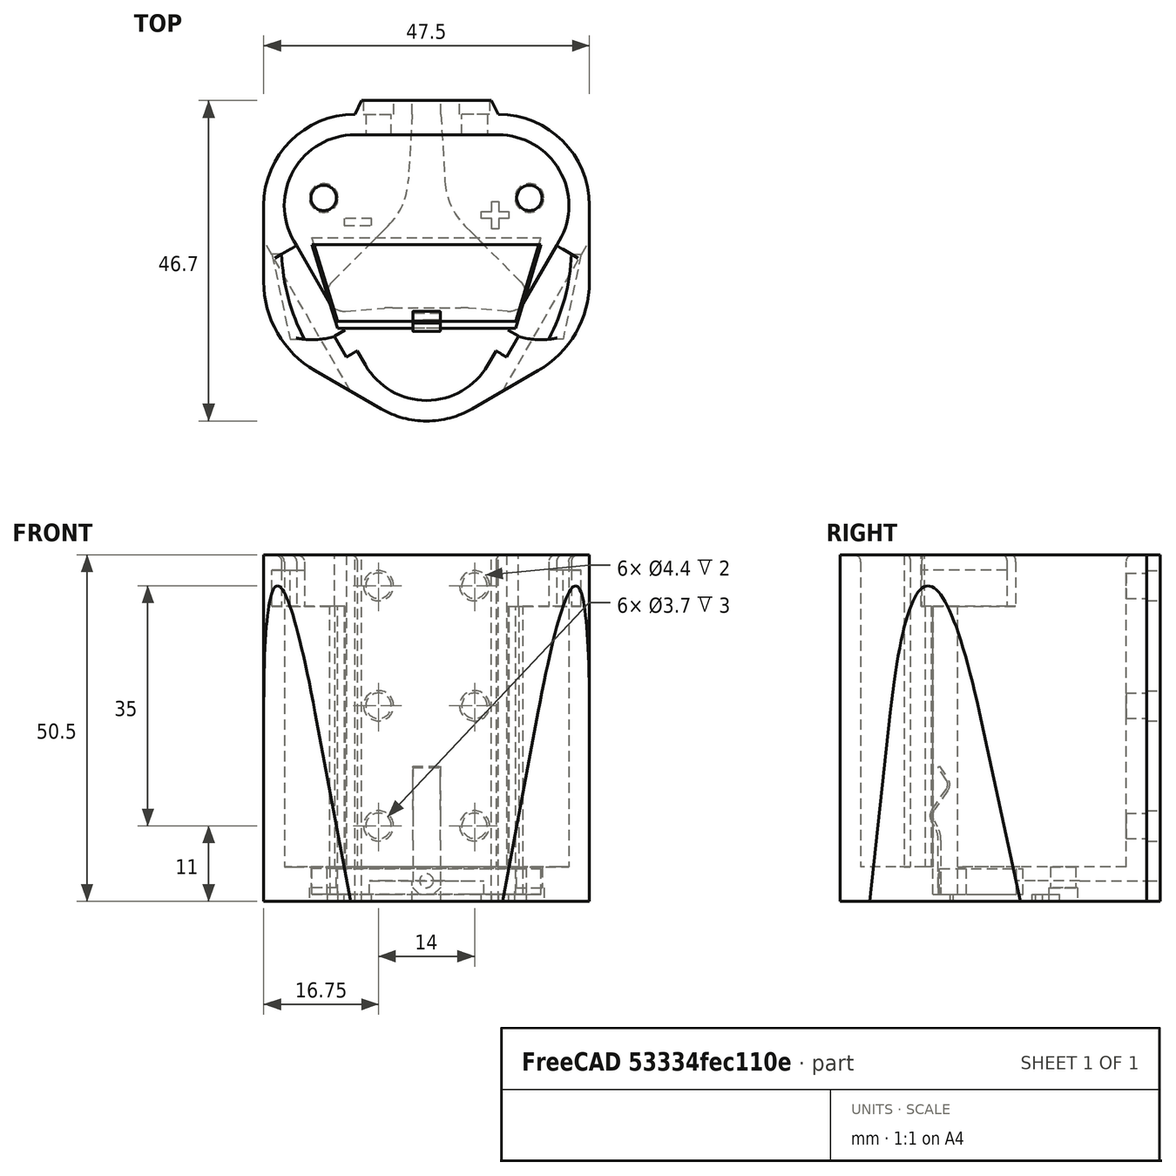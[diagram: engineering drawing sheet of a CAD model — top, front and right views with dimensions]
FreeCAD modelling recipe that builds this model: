
FCSTD DOCUMENT  (FreeCAD 1.0R39319 (Git))
Label: support_batterie_parkside_12V
License: All rights reserved
LicenseURL: https://en.wikipedia.org/wiki/All_rights_reserved
objects: Sketcher::SketchObject×15, PartDesign::Pocket×14, PartDesign::Pad×4, Mesh::Feature×4, PartDesign::Body×3, App::Part×3, PartDesign::Chamfer×2, PartDesign::Mirrored×2, App::LinkElement×2, App::Link×1, PartDesign::SubShapeBinder×1, PartDesign::LinearPattern×1, PartDesign::Fillet×1
note: 103 computed .brp shape members not serialized (recipe doc carries the construction recipe); baked Part::Feature solids carry a one-line shape summary decoded from their .brp

FEATURE [Sketcher::SketchObject] Sketch
  ArcFitTolerance = 1e-06
  AttachmentSupport = -> [XY_Plane003]
  FullyConstrained = true
  MakeInternals = false
  MapMode = 5
  expr: Constraints[10] = 26 / 2
  expr: Constraints[9] = 33.4 / 2
  sketch-geometry (4):
    g0: LineSegment StartX=0 StartY=0 StartZ=0 EndX=-13 EndY=0 EndZ=0
    g1: LineSegment StartX=-13 StartY=0 StartZ=0 EndX=-16.7 EndY=12.2 EndZ=0
    g2: LineSegment StartX=-16.7 StartY=12.2 StartZ=0 EndX=0 EndY=12.2 EndZ=0
    g3: LineSegment StartX=0 StartY=12.2 StartZ=0 EndX=0 EndY=0 EndZ=0
  constraints (11):
    c: Coincident(g-1,g0)
    c: PointOnObject(g0,g-1)
    c: Coincident(g0,g1)
    c: Coincident(g1,g2)
    c: PointOnObject(g2,g-2)
    c: Horizontal(g2)
    c: Coincident(g2,g3)
    c: Coincident(g3,g0)
    c: DistanceY(g3,g3) = 12.2
    c: DistanceX(g2,g2) = 16.7
    c: DistanceX(g0,g0) = 13
FEATURE [PartDesign::Pad] Pad
  Direction = (0,0,1)
  Length = 3.8
  Length2 = 10
  Profile = -> Sketch
  ReferenceAxis = -> Sketch [N_Axis]
  Suppressed = false
  Type = 0
FEATURE [Sketcher::SketchObject] Sketch001
  ArcFitTolerance = 1e-06
  AttachmentSupport = -> [YZ_Plane004]
  FullyConstrained = true
  MakeInternals = false
  MapMode = 5
  Placement = pos=(0,0,0) rot=(0.57735,0.57735,0.57735;2.0944rad)
  sketch-geometry (22):
    g0: LineSegment StartX=-0.2 StartY=0 StartZ=0 EndX=-0.2 EndY=7.9282 EndZ=0
    g1: LineSegment StartX=-0.735898 StartY=9.9282 StartZ=0 EndX=-1.2 EndY=10.7321 EndZ=0
    g2: LineSegment StartX=-1.12969 StartY=12.3424 StartZ=0 EndX=0.965775 EndY=15.335 EndZ=0
    g3: LineSegment StartX=0.980132 StartY=16.6827 StartZ=0 EndX=-0.255119 EndY=18.5293 EndZ=0
    g4: LineSegment StartX=-0.255119 StartY=18.5293 StartZ=0 EndX=0 EndY=18.7 EndZ=0
    g5: LineSegment StartX=0 StartY=18.7 StartZ=0 EndX=1.23525 EndY=16.8534 EndZ=0
    g6: LineSegment StartX=1.2172 StartY=15.159 StartZ=0 EndX=-0.728007 EndY=12.381 EndZ=0
    g7: LineSegment StartX=-0.8 StartY=10.7321 StartZ=0 EndX=-0.335898 EndY=9.9282 EndZ=0
    g8: LineSegment StartX=0.2 StartY=7.9282 StartZ=0 EndX=0.2 EndY=0 EndZ=0
    g9: LineSegment StartX=-0.2 StartY=0 StartZ=0 EndX=0.2 EndY=0 EndZ=0
    g10: ArcOfCircle CenterX=-3.8 CenterY=7.9282 CenterZ=0 NormalX=0 NormalY=0 NormalZ=1 AngleXU=0 Radius=4 StartAngle=0 EndAngle=0.523599
    g11: GeomPoint [constr] X=0.2 Y=9 Z=0
    g12: ArcOfCircle CenterX=-4.2 CenterY=7.9282 CenterZ=0 NormalX=0 NormalY=0 NormalZ=1 AngleXU=0 Radius=4 StartAngle=1e-16 EndAngle=0.523599
    g13: GeomPoint [constr] X=-0.2 Y=9 Z=0
    g14: ArcOfCircle CenterX=0.530127 CenterY=11.5 CenterZ=0 NormalX=0 NormalY=0 NormalZ=1 AngleXU=0 Radius=1.5359 StartAngle=2.53073 EndAngle=3.66519
    g15: GeomPoint [constr] X=-1.28924 Y=11.5794 Z=0
    g16: ArcOfCircle CenterX=0.0990381 CenterY=11.4821 CenterZ=0 NormalX=0 NormalY=0 NormalZ=1 AngleXU=0 Radius=1.5 StartAngle=2.53073 EndAngle=3.66519
    g17: GeomPoint [constr] X=-1.6778 Y=11.5596 Z=0
    g18: ArcOfCircle CenterX=-0.0115278 CenterY=16.0194 CenterZ=0 NormalX=0 NormalY=0 NormalZ=1 AngleXU=0 Radius=1.5 StartAngle=5.67232 EndAngle=6.87274
    g19: GeomPoint [constr] X=1.80608 Y=16 Z=0
    g20: ArcOfCircle CenterX=-0.0115278 CenterY=16.0194 CenterZ=0 NormalX=0 NormalY=0 NormalZ=1 AngleXU=0 Radius=1.19307 StartAngle=5.67232 EndAngle=6.87274
    g21: GeomPoint [constr] X=1.43415 Y=16.004 Z=0
  constraints (53):
    c: PointOnObject(g0,g-1)
    c: Vertical(g0)
    c: Coincident(g3,g4)
    c: Coincident(g4,g5)
    c: Vertical(g8)
    c: Coincident(g0,g9)
    c: Coincident(g9,g8)
    c: Symmetric(g8,g0,g-1)
    c: Horizontal(g11,g13)
    c: PointOnObject(g11,g7)
    c: PointOnObject(g11,g8)
    c: Tangent(g7,g10) = 1.5708
    c: Tangent(g8,g10) = 1.5708
    c: PointOnObject(g13,g1)
    c: PointOnObject(g13,g0)
    c: Tangent(g1,g12) = -1.5708
    c: Tangent(g0,g12) = -1.5708
    c: PointOnObject(g15,g6)
    c: PointOnObject(g15,g7)
    c: Tangent(g6,g14) = -1.5708
    c: Tangent(g7,g14) = -1.5708
    c: PointOnObject(g17,g2)
    c: PointOnObject(g17,g1)
    c: Tangent(g2,g16) = 1.5708
    c: Tangent(g1,g16) = 1.5708
    c: PointOnObject(g19,g5)
    c: PointOnObject(g19,g6)
    c: Tangent(g5,g18) = 1.5708
    c: Tangent(g6,g18) = 1.5708
    c: PointOnObject(g21,g3)
    c: PointOnObject(g21,g2)
    c: Tangent(g3,g20) = -1.5708
    c: Tangent(g2,g20) = -1.5708
    c: Perpendicular(g3,g4)
    c: Equal(g5,g3)
    c: Equal(g7,g1)
    c: Equal(g8,g0)
    c: DistanceY(g0,g4) = 18.7
    c: DistanceY(g-1,g11) = 9
    c: Parallel(g6,g2)
    c: Parallel(g1,g7)
    c: DistanceX(g9,g9) = 0.4
    c: Horizontal(g18,g20)
    c: Perpendicular(g4,g5)
    c: PointOnObject(g4,g-2)
    c: Radius(g18) = 1.5
    c: Radius(g16) = 1.5
    c: Radius(g10) = 4
    c: DistanceY(g-1,g14) = 11.5
    c: DistanceY(g-1,g19) = 16
    c: DistanceX(g1,g-1) = 1.2
    c: Angle(g1,g0) = 2.61799
    c: Angle(g7,g6) = 2.00713
FEATURE [PartDesign::Pad] Pad001
  Direction = (1,0,0)
  Length = 4
  Length2 = 10
  Midplane = true
  Placement = pos=(0,0,0) rot=(1,1,1;2.0944rad)
  Profile = -> Sketch001
  ReferenceAxis = -> Sketch001 [N_Axis]
  Suppressed = false
  Type = 0
FEATURE [Sketcher::SketchObject] Sketch002
  ArcFitTolerance = 1e-06
  AttachmentSupport = -> [Pad001]
  FullyConstrained = true
  MakeInternals = false
  MapMode = 5
  Placement = pos=(0,0.2,0) rot=(0.57735,0.57735,0.57735;4.18879rad)
  sketch-geometry (1):
    g0: Circle CenterX=2 CenterY=0 CenterZ=0 NormalX=0 NormalY=0 NormalZ=1 AngleXU=0 Radius=1
  constraints (3):
    c: PointOnObject(g0,g-1)
    c: Diameter(g0) = 2
    c: DistanceX(g-1,g0) = 2
FEATURE [PartDesign::Pocket] Pocket
  BaseFeature = -> Pad001
  Direction = (0,-1,0)
  Length = 5
  Length2 = 5
  Placement = pos=(0,0,0) rot=(1,1,1;2.0944rad)
  Profile = -> Sketch002
  ReferenceAxis = -> Sketch002 [N_Axis]
  Suppressed = false
  Type = 0
FEATURE [PartDesign::Chamfer] Chamfer
  Angle = 45
  Base = -> Pocket [Edge23,Edge9]
  BaseFeature = -> Pocket
  ChamferType = 0
  FlipDirection = false
  Placement = pos=(0,0,0) rot=(1,1,1;2.0944rad)
  Size = 1
  Size2 = 1
  SupportTransform = false
  Suppressed = false
  UseAllEdges = false
FEATURE [PartDesign::Body] Body001  label="electrode"
  AllowCompound = false
  Group = -> [Sketch001,Pad001,Sketch002,Pocket,Chamfer]
  Origin = -> Origin004
  Tip = -> Chamfer
FEATURE [PartDesign::Mirrored] Mirrored
  BaseFeature = -> Pad
  MirrorPlane = -> Sketch [V_Axis]
  Originals = -> [Pad]
  Refine = true
  Suppressed = false
  TransformMode = 0
FEATURE [PartDesign::Body] Body  label="plastique"
  AllowCompound = false
  Group = -> [Sketch,Pad,Mirrored]
  Origin = -> Origin003
  Tip = -> Mirrored
FEATURE [App::LinkElement] Link_i0
  LinkPlacement = pos=(-12,5,0) rot=(0,0,-1;1.0472rad)
  LinkedObject = -> Body001
  Placement = pos=(-12,5,0) rot=(0,0,-1;1.0472rad)
  _LinkOwner = 4285
FEATURE [App::LinkElement] Link_i1
  LinkPlacement = pos=(12,5,0) rot=(0,0,1;1.0472rad)
  LinkedObject = -> Body001
  Placement = pos=(12,5,0) rot=(0,0,1;1.0472rad)
  _LinkOwner = 4285
FEATURE [App::Link] Link  label="electrode001"
  ElementCount = 2
  ElementList = -> [Link_i0,Link_i1]
  LinkPlacement = pos=(0,0,-4) rot=(0,0,1;0rad)
  LinkedObject = -> Body001
  Placement = pos=(0,0,-4) rot=(0,0,1;0rad)
FEATURE [App::Part] Part001  label="connecteur_aliexpress"
  Group = -> [Body,Body001,Link]
  Origin = -> Origin002
  Placement = pos=(0,-1,0) rot=(0,0,1;0rad)
FEATURE [Sketcher::SketchObject] Sketch003
  ArcFitTolerance = 1e-06
  AttachmentOffset = pos=(0,0,4) rot=(0,0,1;0rad)
  AttachmentSupport = -> [XY_Plane005]
  FullyConstrained = true
  MakeInternals = false
  MapMode = 5
  Placement = pos=(0,0,4) rot=(0,0,1;0rad)
  sketch-geometry (6):
    g0: LineSegment StartX=0 StartY=27.1999 StartZ=0 EndX=-10.45 EndY=27.1999 EndZ=0
    g1: ArcOfCircle CenterX=-10.45 CenterY=16.8999 CenterZ=0 NormalX=0 NormalY=0 NormalZ=1 AngleXU=0 Radius=10.3 StartAngle=1.5708 EndAngle=3.66519
    g2: LineSegment StartX=-19.3701 StartY=11.7499 StartZ=0 EndX=-8.92006 EndY=-6.35 EndZ=0
    g3: ArcOfCircle CenterX=1.3e-15 CenterY=-1.2 CenterZ=0 NormalX=0 NormalY=0 NormalZ=1 AngleXU=0 Radius=10.3 StartAngle=3.66519 EndAngle=4.71239
    g4: LineSegment StartX=-6e-16 StartY=-11.5 StartZ=0 EndX=0 EndY=27.1999 EndZ=0
    g5: LineSegment [constr] StartX=-6e-16 StartY=-11.5 StartZ=0 EndX=-8.92006 EndY=-11.5 EndZ=0
  constraints (16):
    c: PointOnObject(g0,g-2)
    c: Horizontal(g0)
    c: Tangent(g0,g1) = -1.5708
    c: Tangent(g1,g2) = -1.5708
    c: Tangent(g2,g3) = -1.5708
    c: PointOnObject(g3,g-2)
    c: Coincident(g3,g4)
    c: Coincident(g4,g0)
    c: Angle(g2,g-1) = 1.0472
    c: Equal(g1,g3)
    c: Radius(g1) = 10.3
    c: Horizontal(g5)
    c: Vertical(g5,g2)
    c: Tangent(g5,g3) = 1.5708
    c: Distance(g2,g2) = 20.9
    c: DistanceY(g3,g-1) = 11.5
FEATURE [Sketcher::SketchObject] Sketch004
  ArcFitTolerance = 1e-06
  AttachmentSupport = -> [XY_Plane005]
  ExternalGeometry = -> [Sketch003]
  FullyConstrained = true
  MakeInternals = false
  MapMode = 5
  sketch-geometry (10):
    g0: LineSegment StartX=0 StartY=30.1999 StartZ=0 EndX=-10.45 EndY=30.1999 EndZ=0
    g1: ArcOfCircle CenterX=-10.45 CenterY=16.8999 CenterZ=0 NormalX=0 NormalY=0 NormalZ=1 AngleXU=0 Radius=13.3 StartAngle=1.5708 EndAngle=3.14159
    g2: ArcOfCircle CenterX=1.3e-15 CenterY=-1.2 CenterZ=0 NormalX=0 NormalY=0 NormalZ=1 AngleXU=0 Radius=13.3 StartAngle=4.18879 EndAngle=4.71239
    g3: LineSegment StartX=0 StartY=30.1999 StartZ=0 EndX=-1.2e-15 EndY=-14.5 EndZ=0
    g4: LineSegment StartX=-23.75 StartY=16.8999 StartZ=0 EndX=-23.75 EndY=5.81481 EndZ=0
    g5: LineSegment StartX=-16.25 StartY=-7.17558 StartZ=0 EndX=-6.65 EndY=-12.7181 EndZ=0
    g6: ArcOfCircle CenterX=-8.75 CenterY=5.81481 CenterZ=0 NormalX=0 NormalY=0 NormalZ=1 AngleXU=0 Radius=15 StartAngle=3.14159 EndAngle=4.18879
    g7: GeomPoint [constr] X=-23.75 Y=-2.84545 Z=0
    g8: LineSegment [constr] StartX=-19.3701 StartY=11.7499 StartZ=0 EndX=-23.75 EndY=16.8999 EndZ=0
    g9: LineSegment [constr] StartX=-8.92006 StartY=-6.35 StartZ=0 EndX=-6.65 EndY=-12.7181 EndZ=0
  constraints (23):
    c: PointOnObject(g0,g-2)
    c: Horizontal(g0)
    c: Tangent(g0,g1) = -1.5708
    c: PointOnObject(g2,g-2)
    c: Coincident(g3,g0)
    c: Coincident(g3,g2)
    c: Coincident(g2,g-7)
    c: Coincident(g1,g-6)
    c: DistanceY(g-5,g0) = 3
    c: Tangent(g5,g2) = -1.5708
    c: Tangent(g4,g1) = -1.5708
    c: PointOnObject(g7,g4)
    c: PointOnObject(g7,g5)
    c: Tangent(g4,g6) = -1.5708
    c: Tangent(g5,g6) = -1.5708
    c: Equal(g5,g4)
    c: Coincident(g8,g-6)
    c: Coincident(g8,g1)
    c: Coincident(g9,g-7)
    c: Coincident(g9,g2)
    c: Equal(g9,g8)
    c: Vertical(g4)
    c: Radius(g6) = 15
FEATURE [PartDesign::Pad] Pad002
  Direction = (0,0,1)
  Length = 49.5
  Length2 = 1
  Profile = -> Sketch004
  ReferenceAxis = -> Sketch004 [N_Axis]
  Suppressed = false
  Type = 4
FEATURE [PartDesign::Pocket] Pocket001
  BaseFeature = -> Pad002
  Direction = (0,0,-1)
  Length = 5
  Length2 = 5
  Profile = -> Sketch003
  ReferenceAxis = -> Sketch003 [N_Axis]
  Reversed = true
  Suppressed = false
  Type = 1
FEATURE [Sketcher::SketchObject] Sketch005
  ArcFitTolerance = 1e-06
  AttachmentOffset = pos=(0,0,1) rot=(0,0,1;0rad)
  AttachmentSupport = -> [XY_Plane005]
  FullyConstrained = true
  MakeInternals = false
  MapMode = 5
  Placement = pos=(0,0,-1) rot=(0,1,0;3.14159rad)
  sketch-geometry (11):
    g0: ArcOfCircle CenterX=12 CenterY=4 CenterZ=0 NormalX=0 NormalY=0 NormalZ=1 AngleXU=0 Radius=2.5 StartAngle=4.63328 EndAngle=7.06858
    g1: LineSegment StartX=11.8024 StartY=1.50782 StartZ=0 EndX=6.18535 EndY=1.95309 EndZ=0
    g2: LineSegment StartX=5 StartY=2 StartZ=0 EndX=0 EndY=2 EndZ=0
    g3: LineSegment StartX=13.7678 StartY=5.76777 StartZ=0 EndX=5.58287 EndY=13.9527 EndZ=0
    g4: LineSegment StartX=0 StartY=32 StartZ=0 EndX=0 EndY=2 EndZ=0
    g5: ArcOfCircle CenterX=5 CenterY=-13 CenterZ=0 NormalX=0 NormalY=0 NormalZ=1 AngleXU=0 Radius=15 StartAngle=1.49169 EndAngle=1.5708
    g6: GeomPoint [constr] X=5.5936 Y=2 Z=0
    g7: LineSegment StartX=0 StartY=32 StartZ=0 EndX=2 EndY=32 EndZ=0
    g8: LineSegment StartX=2 StartY=32 StartZ=0 EndX=2.67074 EndY=20.4443 EndZ=0
    g9: ArcOfCircle CenterX=12.6539 CenterY=21.0237 CenterZ=0 NormalX=0 NormalY=0 NormalZ=1 AngleXU=0 Radius=10 StartAngle=3.19957 EndAngle=3.92699
    g10: GeomPoint [constr] X=2.89131 Y=16.6442 Z=0
  constraints (28):
    c: PointOnObject(g2,g-2)
    c: Horizontal(g2)
    c: Coincident(g4,g2)
    c: Tangent(g3,g0) = -1.5708
    c: PointOnObject(g6,g2)
    c: PointOnObject(g6,g1)
    c: Tangent(g2,g5) = -1.5708
    c: Tangent(g1,g5) = -1.5708
    c: DistanceY(g-1,g0) = 4
    c: DistanceX(g-1,g0) = 12
    c: Radius(g0) = 2.5
    c: Tangent(g1,g0) = 1.5708
    c: PointOnObject(g4,g-2)
    c: Coincident(g7,g4)
    c: Horizontal(g7)
    c: Coincident(g8,g7)
    c: PointOnObject(g10,g8)
    c: PointOnObject(g10,g3)
    c: Tangent(g8,g9) = -1.5708
    c: Tangent(g3,g9) = 1.5708
    c: DistanceY(g4,g4) = 30
    c: DistanceY(g-1,g2) = 2
    c: DistanceX(g7,g7) = 2
    c: Angle(g3,g-1) = 0.785398
    c: Radius(g9) = 10
    c: Equal(g3,g8)
    c: Radius(g5) = 15
    c: DistanceX(g2,g2) = 5
FEATURE [PartDesign::SubShapeBinder] Binder
  BindCopyOnChange = 0
  BindMode = 0
  ClaimChildren = false
  Context = -> Part [Body002.Binder.]
  Fuse = false
  MakeFace = true
  OffsetFill = false
  OffsetIntersection = false
  OffsetJoinType = 0
  OffsetOpenResult = false
  PartialLoad = false
  Relative = true
  Support = -> [Part001[Body.Mirrored.Face4]]
  _Version = 2
FEATURE [PartDesign::Pocket] Pocket003
  BaseFeature = -> Pocket001
  Direction = (0,0,1)
  Length = 8
  Length2 = 5
  Profile = -> Binder
  Suppressed = false
  Type = 1
FEATURE [PartDesign::Pocket] Pocket004
  BaseFeature = -> Pocket003
  Direction = (0,0,1)
  Length = 5
  Length2 = 5
  Offset = 2
  Profile = -> Sketch005
  ReferenceAxis = -> Sketch005 [N_Axis]
  Suppressed = false
  Type = 2
FEATURE [PartDesign::Pocket] Pocket005
  BaseFeature = -> Pocket004
  Direction = (0,0,1)
  Length = 5
  Length2 = 5
  Profile = -> Pocket004 [Face29]
  Suppressed = false
  Type = 0
FEATURE [Sketcher::SketchObject] Sketch006
  ArcFitTolerance = 1e-06
  AttachmentSupport = -> [Pocket005]
  FullyConstrained = true
  MakeInternals = false
  MapMode = 5
  Placement = pos=(0,0,49.5) rot=(0,0,1;0rad)
  sketch-geometry (5):
    g0: LineSegment StartX=-18.9701 StartY=11.0571 StartZ=0 EndX=-21.1351 EndY=9.80711 EndZ=0
    g1: ArcOfCircle CenterX=-16.6525 CenterY=8.33999 CenterZ=0 NormalX=0 NormalY=0 NormalZ=1 AngleXU=0 Radius=11 StartAngle=4.60788 EndAngle=5.03941
    g2: LineSegment StartX=-13.1191 StartY=-2.07705 StartZ=0 EndX=-11.8201 EndY=-1.32705 EndZ=0
    g3: LineSegment StartX=-11.8201 StartY=-1.32705 StartZ=0 EndX=-18.9701 EndY=11.0571 EndZ=0
    g4: ArcOfCircle CenterX=7.84255 CenterY=10.9447 CenterZ=0 NormalX=0 NormalY=0 NormalZ=1 AngleXU=0 Radius=29 StartAngle=3.18083 EndAngle=3.62755
  constraints (17):
    c: Coincident(g1,g2)
    c: Coincident(g2,g3)
    c: Coincident(g3,g0)
    c: PointOnObject(g0,g-3)
    c: Perpendicular(g-3,g0)
    c: Distance(g0,g0) = 2.5
    c: Distance(g3,g3) = 14.3
    c: Distance(g2,g-3) = 5.8
    c: Perpendicular(g3,g2)
    c: PointOnObject(g2,g-3)
    c: Distance(g2,g2) = 1.5
    c: Coincident(g4,g0)
    c: Coincident(g4,g1)
    c: DistanceX(g1,g-1) = 17.8
    c: DistanceY(g1,g-1) = 2.6
    c: Radius(g4) = 29
    c: Radius(g1) = 11
FEATURE [PartDesign::Pocket] Pocket006
  BaseFeature = -> Pocket005
  Direction = (0,0,-1)
  Length = 7.5
  Length2 = 5
  Profile = -> Sketch006
  ReferenceAxis = -> Sketch006 [N_Axis]
  Suppressed = false
  Type = 0
FEATURE [Sketcher::SketchObject] Sketch007
  ArcFitTolerance = 1e-06
  AttachmentSupport = -> [Pocket006]
  ExternalGeometry = -> [Pocket006]
  FullyConstrained = true
  MakeInternals = false
  MapMode = 5
  Placement = pos=(0,0,49.5) rot=(0,0,1;0rad)
  sketch-geometry (4):
    g0: LineSegment StartX=-13.4289 StartY=-2.14045 StartZ=0 EndX=-11.6789 EndY=-5.17154 EndZ=0
    g1: LineSegment StartX=-11.6789 StartY=-5.17154 StartZ=0 EndX=-10.1201 EndY=-4.27154 EndZ=0
    g2: LineSegment StartX=-10.1201 StartY=-4.27154 StartZ=0 EndX=-11.8701 EndY=-1.24045 EndZ=0
    g3: LineSegment StartX=-11.8701 StartY=-1.24045 StartZ=0 EndX=-13.4289 EndY=-2.14045 EndZ=0
  constraints (12):
    c: Coincident(g0,g1)
    c: Coincident(g1,g2)
    c: Coincident(g2,g3)
    c: Coincident(g3,g0)
    c: Parallel(g0,g2)
    c: Parallel(g1,g3)
    c: Perpendicular(g0,g1)
    c: Distance(g3,g3) = 1.8
    c: Distance(g2,g2) = 3.5
    c: PointOnObject(g2,g-3)
    c: Distance(g-3,g2) = 0.1
    c: PointOnObject(g1,g-3)
FEATURE [PartDesign::Pocket] Pocket007
  BaseFeature = -> Pocket006
  Direction = (0,0,-1)
  Length = 45.5
  Length2 = 5
  Profile = -> Sketch007
  ReferenceAxis = -> Sketch007 [N_Axis]
  Suppressed = false
  Type = 0
FEATURE [Sketcher::SketchObject] Sketch008
  ArcFitTolerance = 1e-06
  AttachmentSupport = -> [Pocket007]
  ExternalGeometry = -> [Pocket007]
  FullyConstrained = true
  MakeInternals = false
  MapMode = 5
  Placement = pos=(0,0,42) rot=(0,0,1;0rad)
  sketch-geometry (4):
    g0: LineSegment StartX=-21.1351 StartY=9.80711 StartZ=0 EndX=-22.5351 EndY=9.80711 EndZ=0
    g1: LineSegment StartX=-22.5351 StartY=9.80711 StartZ=0 EndX=-19.9 EndY=-2.6 EndZ=0
    g2: LineSegment StartX=-19.9 StartY=-2.6 StartZ=0 EndX=-17.8 EndY=-2.6 EndZ=0
    g3: LineSegment StartX=-21.1351 StartY=9.80711 StartZ=0 EndX=-17.8 EndY=-2.6 EndZ=0
  constraints (10):
    c: Horizontal(g0)
    c: Coincident(g1,g0)
    c: Coincident(g2,g1)
    c: Horizontal(g2)
    c: DistanceX(g0,g0) = 1.4
    c: DistanceX(g2,g2) = 2.1
    c: Coincident(g3,g0)
    c: Coincident(g3,g2)
    c: Coincident(g2,g-3)
    c: Coincident(g0,g-3)
FEATURE [PartDesign::Pocket] Pocket008
  BaseFeature = -> Pocket007
  Direction = (0,0,-1)
  Length = 5.3
  Length2 = 5
  Profile = -> Sketch008
  ReferenceAxis = -> Sketch008 [N_Axis]
  Reversed = true
  Suppressed = false
  Type = 0
FEATURE [Mesh::Feature] ACCUMULATOR_Bottom_Cover
FEATURE [Mesh::Feature] ACCUMULATOR_Bottom_Plate
FEATURE [Mesh::Feature] ACCUMULATOR_Top_Cover
FEATURE [Mesh::Feature] ACCUMULATOR_Top_Plate
FEATURE [App::Part] Part003  label="Batterie"
  Group = -> [ACCUMULATOR_Bottom_Cover,ACCUMULATOR_Bottom_Plate,ACCUMULATOR_Top_Cover,ACCUMULATOR_Top_Plate]
  Origin = -> Origin008
  Placement = pos=(0,1,85) rot=(-0.707107,-0.707107,0;3.14159rad)
FEATURE [Sketcher::SketchObject] Sketch010
  ArcFitTolerance = 1e-06
  AttachmentSupport = -> [Pocket008]
  FullyConstrained = true
  MakeInternals = false
  MapMode = 5
  Placement = pos=(0,0,-1) rot=(1,0,0;3.14159rad)
  sketch-geometry (1):
    g0: Circle CenterX=-15 CenterY=-18 CenterZ=0 NormalX=0 NormalY=0 NormalZ=1 AngleXU=0 Radius=2.1
  constraints (3):
    c: Diameter(g0) = 4.2
    c: Distance(g0,g-2) = 15
    c: DistanceY(g0,g-1) = 18
FEATURE [PartDesign::Pocket] Pocket010
  BaseFeature = -> Pocket008
  Direction = (0,0,1)
  Length = 2
  Length2 = 5
  Profile = -> Sketch010
  ReferenceAxis = -> Sketch010 [N_Axis]
  Suppressed = false
  Type = 0
FEATURE [Sketcher::SketchObject] Sketch011
  ArcFitTolerance = 1e-06
  AttachmentSupport = -> [Pocket010]
  ExternalGeometry = -> [Pocket010]
  FullyConstrained = true
  MakeInternals = false
  MapMode = 5
  Placement = pos=(0,0,1) rot=(1,0,0;3.14159rad)
  sketch-geometry (1):
    g0: Circle CenterX=-15 CenterY=-18 CenterZ=0 NormalX=0 NormalY=0 NormalZ=1 AngleXU=0 Radius=1.85
  constraints (2):
    c: Diameter(g0) = 3.7
    c: Coincident(g0,g-3)
FEATURE [PartDesign::Pocket] Pocket011
  BaseFeature = -> Pocket010
  Direction = (0,0,1)
  Length = 5
  Length2 = 5
  Profile = -> Sketch011
  ReferenceAxis = -> Sketch011 [N_Axis]
  Suppressed = false
  Type = 0
FEATURE [PartDesign::Pad] Pad003
  BaseFeature = -> Pocket011
  Direction = (0,1,0)
  Length = 2
  Length2 = 10
  Profile = -> Pocket011 [Face1]
  Suppressed = false
  Type = 0
FEATURE [PartDesign::Chamfer] Chamfer001
  Angle = 45
  Base = -> Pad003 [Edge57]
  BaseFeature = -> Pad003
  ChamferType = 1
  FlipDirection = false
  Size = 1
  Size2 = 1.99
  SupportTransform = false
  Suppressed = false
  UseAllEdges = false
FEATURE [Sketcher::SketchObject] Sketch012
  ArcFitTolerance = 1e-06
  AttachmentSupport = -> [Chamfer001]
  FullyConstrained = true
  MakeInternals = false
  MapMode = 5
  Placement = pos=(0,32.1999,0) rot=(0,0.707107,0.707107;3.14159rad)
  sketch-geometry (1):
    g0: Circle CenterX=7 CenterY=10 CenterZ=0 NormalX=0 NormalY=0 NormalZ=1 AngleXU=0 Radius=2.2
  constraints (3):
    c: Diameter(g0) = 4.4
    c: DistanceY(g-1,g0) = 10
    c: DistanceX(g-1,g0) = 7
FEATURE [PartDesign::Pocket] Pocket012
  BaseFeature = -> Chamfer001
  Direction = (0,-1,2e-16)
  Length = 2
  Length2 = 5
  Profile = -> Sketch012
  ReferenceAxis = -> Sketch012 [N_Axis]
  Suppressed = false
  Type = 0
FEATURE [Sketcher::SketchObject] Sketch013
  ArcFitTolerance = 1e-06
  AttachmentSupport = -> [Pocket012]
  ExternalGeometry = -> [Sketch012]
  FullyConstrained = true
  MakeInternals = false
  MapMode = 5
  Placement = pos=(0,32.1999,0) rot=(0,0.707107,0.707107;3.14159rad)
  sketch-geometry (1):
    g0: Circle CenterX=7 CenterY=10 CenterZ=0 NormalX=0 NormalY=0 NormalZ=1 AngleXU=0 Radius=1.85
  constraints (2):
    c: Diameter(g0) = 3.7
    c: Coincident(g0,g-3)
FEATURE [PartDesign::Pocket] Pocket013
  BaseFeature = -> Pocket012
  Direction = (0,-1,2e-16)
  Length = 5
  Length2 = 5
  Profile = -> Sketch013
  ReferenceAxis = -> Sketch013 [N_Axis]
  Suppressed = false
  Type = 0
FEATURE [PartDesign::LinearPattern] LinearPattern
  BaseFeature = -> Pocket013
  Direction = -> Sketch012 [V_Axis]
  Length = 35
  Mode = 0
  Occurrences = 3
  Offset = 17.5
  Originals = -> [Pocket012,Pocket013]
  Suppressed = false
  TransformMode = 0
FEATURE [Sketcher::SketchObject] Sketch014
  ArcFitTolerance = 1e-06
  AttachmentOffset = pos=(0,0,0) rot=(0,1,0;0.523599rad)
  AttachmentSupport = -> [XZ_Plane005]
  ExternalGeometry = -> [LinearPattern]
  FullyConstrained = true
  MakeInternals = false
  MapMode = 5
  Placement = pos=(0,0,0) rot=(0.935113,0.250563,0.250563;1.63783rad)
  sketch-geometry (3):
    g0: LineSegment StartX=-19.6703 StartY=45 StartZ=0 EndX=-19.6703 EndY=-1 EndZ=0
    g1: LineSegment StartX=-19.6703 StartY=45 StartZ=0 EndX=-14.6703 EndY=-1 EndZ=0
    g2: LineSegment StartX=-19.6703 StartY=-1 StartZ=0 EndX=-14.6703 EndY=-1 EndZ=0
  constraints (9):
    c: Coincident(g1,g0)
    c: Coincident(g2,g0)
    c: Coincident(g2,g1)
    c: Horizontal(g2)
    c: DistanceX(g2,g2) = 5
    c: DistanceY(g-1,g0) = 45
    c: Vertical(g-3,g0)
    c: Vertical(g0)
    c: DistanceY(g0,g-1) = 1
FEATURE [PartDesign::Pocket] Pocket014
  BaseFeature = -> LinearPattern
  Direction = (-0.5,0.866025,-1e-16)
  Length = 5
  Length2 = 5
  Midplane = true
  Profile = -> Sketch014
  ReferenceAxis = -> Sketch014 [N_Axis]
  Suppressed = false
  Type = 1
FEATURE [PartDesign::Mirrored] Mirrored001
  BaseFeature = -> Pocket014
  MirrorPlane = -> Sketch008 [V_Axis]
  Originals = -> [Pocket008]
  Refine = true
  Suppressed = false
  TransformMode = 1
FEATURE [Sketcher::SketchObject] Sketch009
  ArcFitTolerance = 1e-06
  AttachmentSupport = -> [Mirrored001]
  FullyConstrained = true
  MakeInternals = false
  MapMode = 5
  Placement = pos=(0,0,-1) rot=(1,0,0;3.14159rad)
  sketch-geometry (16):
    g0: LineSegment StartX=-12 StartY=-15 StartZ=0 EndX=-12 EndY=-14 EndZ=0
    g1: LineSegment StartX=-12 StartY=-14 StartZ=0 EndX=-8 EndY=-14 EndZ=0
    g2: LineSegment StartX=-8 StartY=-14 StartZ=0 EndX=-8 EndY=-15 EndZ=0
    g3: LineSegment StartX=-8 StartY=-15 StartZ=0 EndX=-12 EndY=-15 EndZ=0
    g4: LineSegment StartX=9.5 StartY=-13.5 StartZ=0 EndX=9.5 EndY=-15 EndZ=0
    g5: LineSegment StartX=9.5 StartY=-17.5 StartZ=0 EndX=10.5 EndY=-17.5 EndZ=0
    g6: LineSegment StartX=10.5 StartY=-17.5 StartZ=0 EndX=10.5 EndY=-16 EndZ=0
    g7: LineSegment StartX=10.5 StartY=-13.5 StartZ=0 EndX=9.5 EndY=-13.5 EndZ=0
    g8: LineSegment StartX=8 StartY=-15 StartZ=0 EndX=8 EndY=-16 EndZ=0
    g9: LineSegment StartX=8 StartY=-16 StartZ=0 EndX=9.5 EndY=-16 EndZ=0
    g10: LineSegment StartX=12 StartY=-16 StartZ=0 EndX=12 EndY=-15 EndZ=0
    g11: LineSegment StartX=12 StartY=-15 StartZ=0 EndX=10.5 EndY=-15 EndZ=0
    g12: LineSegment StartX=10.5 StartY=-15 StartZ=0 EndX=10.5 EndY=-13.5 EndZ=0
    g13: LineSegment StartX=9.5 StartY=-16 StartZ=0 EndX=9.5 EndY=-17.5 EndZ=0
    g14: LineSegment StartX=9.5 StartY=-15 StartZ=0 EndX=8 EndY=-15 EndZ=0
    g15: LineSegment StartX=10.5 StartY=-16 StartZ=0 EndX=12 EndY=-16 EndZ=0
  constraints (49):
    c: Coincident(g0,g1)
    c: Coincident(g1,g2)
    c: Coincident(g2,g3)
    c: Coincident(g3,g0)
    c: Vertical(g0)
    c: Vertical(g2)
    c: Horizontal(g1)
    c: Horizontal(g3)
    c: Coincident(g13,g5)
    c: Coincident(g5,g6)
    c: Coincident(g12,g7)
    c: Coincident(g7,g4)
    c: Vertical(g4)
    c: Vertical(g6)
    c: Horizontal(g5)
    c: Horizontal(g7)
    c: Coincident(g8,g9)
    c: Coincident(g15,g10)
    c: Coincident(g10,g11)
    c: Coincident(g14,g8)
    c: Vertical(g8)
    c: Vertical(g10)
    c: Horizontal(g9)
    c: Horizontal(g11)
    c: PointOnObject(g6,g15)
    c: PointOnObject(g4,g14)
    c: Coincident(g11,g12)
    c: PointOnObject(g14,g4)
    c: Coincident(g9,g13)
    c: PointOnObject(g15,g6)
    c: Equal(g11,g12)
    c: Equal(g12,g4)
    c: Equal(g4,g14)
    c: Equal(g14,g9)
    c: Equal(g9,g13)
    c: Equal(g13,g6)
    c: Equal(g6,g15)
    c: Equal(g7,g8)
    c: Equal(g8,g10)
    c: Equal(g10,g5)
    c: Equal(g5,g0)
    c: Vertical(g13)
    c: Horizontal(g15)
    c: DistanceX(g8,g10) = 4
    c: DistanceY(g10,g10) = 1
    c: DistanceX(g3,g3) = 4
    c: Symmetric(g10,g0,g-2)
    c: DistanceY(g0,g-1) = 15
    c: DistanceX(g1,g-1) = 8
FEATURE [PartDesign::Pocket] Pocket009
  BaseFeature = -> Mirrored001
  Direction = (0,0,1)
  Length = 1
  Length2 = 5
  Profile = -> Sketch009
  ReferenceAxis = -> Sketch009 [N_Axis]
  Suppressed = false
  Type = 0
FEATURE [PartDesign::Fillet] Fillet
  Base = -> Pocket009 [Edge90,Edge81,Edge76,Edge87]
  BaseFeature = -> Pocket009
  Radius = 1
  SupportTransform = false
  Suppressed = false
  UseAllEdges = false
FEATURE [PartDesign::Body] Body002  label="holder"
  AllowCompound = false
  Group = -> [Sketch003,Sketch004,Pad002,Pocket001,Sketch005,Binder,Pocket003,Pocket004,Pocket005,Sketch006,Pocket006,Sketch007,Pocket007,Sketch008,Pocket008,Sketch010,Pocket010,Sketch011,Pocket011,Sketch012,Pad003,Chamfer001,Pocket012,Sketch013,Pocket013,LinearPattern,Sketch014,Pocket014,Mirrored001,Sketch009,Pocket009,Fillet]
  Origin = -> Origin005
  Tip = -> Fillet
FEATURE [App::Part] Part  label="Battery_Holder_PARKSIDE_12V"
  Group = -> [Part001,Body002]
  Origin = -> Origin001
